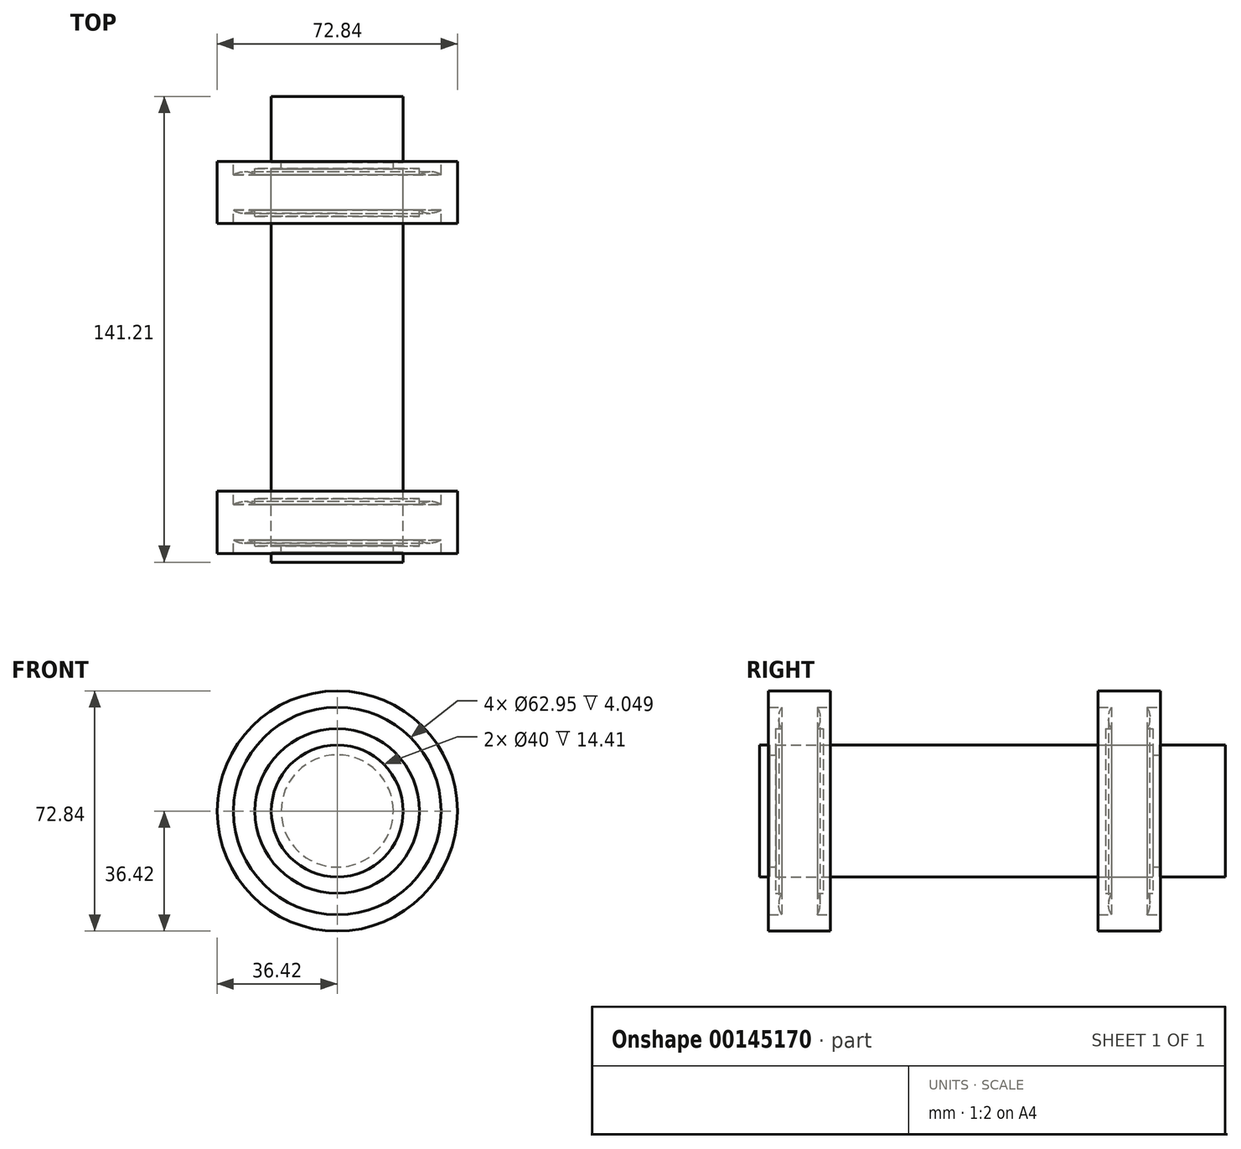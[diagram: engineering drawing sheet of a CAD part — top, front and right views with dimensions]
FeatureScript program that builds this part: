
annotation { "Feature Type Name" : "Feature", "Feature Type Description" : "" }
export const myFeature = defineFeature(function(context is Context, id is Id, definition is map)
    precondition{}
    {
        {
            var Q0;
            Q0=qCreatedBy(makeId("Right.planeOp"),FACE);
            var sketch = newSketch(context, id + "F0", { "sketchPlane" : qUnion([Q0])});
            skLineSegment(sketch, "E0.bottom", {"start": v(-65.09, 24.94) * mm, "end": v(-63.26, 24.94) * mm});
            skLineSegment(sketch, "E0.top", {"start": v(-65.09, 20) * mm, "end": v(-50.68, 20) * mm});
            skLineSegment(sketch, "E0.left", {"start": v(-65.09, 24.94) * mm, "end": v(-65.09, 20) * mm});
            skLineSegment(sketch, "E0.right", {"start": v(-50.68, 24.94) * mm, "end": v(-50.68, 20) * mm});
            skLineSegment(sketch, "E1.bottom", {"start": v(-67.3, 36.42) * mm, "end": v(-48.46, 36.42) * mm});
            skLineSegment(sketch, "E1.top", {"start": v(-67.3, 31.48) * mm, "end": v(-63.26, 31.48) * mm});
            skLineSegment(sketch, "E1.left", {"start": v(-67.3, 36.42) * mm, "end": v(-67.3, 31.48) * mm});
            skLineSegment(sketch, "E1.right", {"start": v(-48.46, 36.42) * mm, "end": v(-48.46, 31.48) * mm});
            skArc(sketch, "E2", {"start": v(-63.26, 31.48) * mm, "mid": v(-64.17, 28.2) * mm, "end": v(-63.26, 24.94) * mm});
            skPoint(sketch, "E2.centerSnap0", {"position": v(-57.88, 24.94) * mm});
            skLineSegment(sketch, "E3", {"start": v(-57.88, 0) * mm, "end": v(-157.88, 0) * mm, "construction": true});
            skLineSegment(sketch, "E4.trimOffspring", {"start": v(-52.5, 31.48) * mm, "end": v(-48.46, 31.48) * mm});
            skArc(sketch, "E5.trimOffspring", {"start": v(-52.5, 24.94) * mm, "mid": v(-51.6, 28.2) * mm, "end": v(-52.5, 31.48) * mm});
            skLineSegment(sketch, "E6.trimOffspring", {"start": v(-52.5, 24.94) * mm, "end": v(-50.68, 24.94) * mm});
            skLineSegment(sketch, "E7", {"start": v(-57.88, 36.42) * mm, "end": v(-57.88, 20) * mm, "construction": true});
            skSolve(sketch);
        }
        {
            var Q0;
            Q0=makeQuery(id+"F0.imprint","IMPRINT",FACE,{"disambiguationData":[TD([[makeQuery(id+"F0.imprint","IMPRINT",EDGE,{"derivedFrom":sQuery(id+"F0.wireOp",EDGE,"E0.bottom")}),-1.0]])]});
            var Q1;
            Q1=sQuery(id+"F0.wireOp",EDGE,"E3");
            revolve(context, id + "F1", {"entities" : qUnion([Q0]), "axis" : qUnion([Q1]), "revolveType" : RevolveType.FULL});
        }
        {
            var Q0;
            Q0=makeQuery(id+"F1.opRevolve","SWEPT_BODY",BODY,{"disambiguationData":[OSD([sQuery(id+"F0.wireOp",EDGE,"E0.bottom"),sQuery(id+"F0.wireOp",EDGE,"E0.top"),sQuery(id+"F0.wireOp",EDGE,"E0.left"),sQuery(id+"F0.wireOp",EDGE,"E0.right"),sQuery(id+"F0.wireOp",EDGE,"E1.bottom"),sQuery(id+"F0.wireOp",EDGE,"E1.top"),sQuery(id+"F0.wireOp",EDGE,"E1.left"),sQuery(id+"F0.wireOp",EDGE,"E1.right"),sQuery(id+"F0.wireOp",EDGE,"E2"),sQuery(id+"F0.wireOp",EDGE,"E4.trimOffspring"),sQuery(id+"F0.wireOp",EDGE,"E5.trimOffspring"),sQuery(id+"F0.wireOp",EDGE,"E6.trimOffspring")])]});
            var Q1;
            Q1=sQuery(id+"F0.wireOp",EDGE,"E3");
            var Q2;
            Q2=sQuery(id+"F0.wireOp",EDGE,"E3");
            transform(context, id + "F2", {"entities" : qUnion([Q0]), "transformType" : TransformType.TRANSLATION_ENTITY, "oppositeDirectionEntity" : false, "transformLine" : qUnion([Q1]), "makeCopy" : true});
        }
        {
            var Q0;
            Q0=qCreatedBy(makeId("Right.planeOp"),FACE);
            var sketch = newSketch(context, id + "F3", { "sketchPlane" : qUnion([Q0])});
            skLineSegment(sketch, "E8", {"start": v(-164.99, 20) * mm, "end": v(-50.78, 20) * mm});
            skLineSegment(sketch, "E9", {"start": v(-165.09, 20) * mm, "end": v(-150.68, 20) * mm, "construction": true});
            skLineSegment(sketch, "E10", {"start": v(-164.99, 20) * mm, "end": v(-164.99, 17) * mm});
            skLineSegment(sketch, "E11", {"start": v(-164.99, 17) * mm, "end": v(-166.99, 17) * mm});
            skLineSegment(sketch, "E12", {"start": v(-166.99, 17) * mm, "end": v(-166.99, 20) * mm});
            skLineSegment(sketch, "E13", {"start": v(-166.99, 20) * mm, "end": v(-169.99, 20) * mm});
            skLineSegment(sketch, "E14", {"start": v(-50.78, 20) * mm, "end": v(-50.78, 17) * mm});
            skLineSegment(sketch, "E15", {"start": v(-50.78, 17) * mm, "end": v(-48.78, 17) * mm});
            skLineSegment(sketch, "E16", {"start": v(-48.78, 17) * mm, "end": v(-48.78, 20) * mm});
            skLineSegment(sketch, "E17", {"start": v(-48.78, 20) * mm, "end": v(-28.78, 20) * mm});
            skLineSegment(sketch, "E18", {"start": v(-169.99, 20) * mm, "end": v(-169.99, 0) * mm});
            skLineSegment(sketch, "E19", {"start": v(-169.99, 0) * mm, "end": v(-28.78, 0) * mm});
            skLineSegment(sketch, "E20", {"start": v(-28.78, 0) * mm, "end": v(-28.78, 20) * mm});
            skSolve(sketch);
        }
        {
            var Q0;
            Q0 = qSketchRegion(id + "F3", true);
            var Q1;
            Q1=sQuery(id+"F0.wireOp",EDGE,"E3");
            revolve(context, id + "F4", {"entities" : qUnion([Q0]), "axis" : qUnion([Q1]), "revolveType" : RevolveType.FULL});
        }
    });
